# Revit family: Legrand Cabinet Plexo³ 12 modules
name_source: partatom
category: Equipement électrique
revit_build: Autodesk Revit 2018 (Build: 20170223_1515(x64)
units: mm (PartAtom-declared; Revit-internal decimal feet)

## family parameters
Basée sur le plan de construction = Non
Configuration du panneau = Deux colonnes, circuits au sein
Cote de connecteur circulaire = Utiliser le diamètre
Couper avec des vides une fois chargée = Non
Numéro OmniClass = 23.80.30.11.17
Partagée = Non
Point de calcul de pièce = Non
Titre OmniClass = Distribution Boards and Control Panels
Toujours verticalement = Oui
Type d'élément = Tableau de raccordement

## types (16) — shared parameters
ETIM Class 6.0 = EC000214
Fabricant = Legrand
General Conditions of Use = https://export.legrand.com
IK = 09
IP = 65
Image du type = Plexo3_12_modules_001922_pw_153883_pz_0.jpg
Material = Polystyrene
Polystyrene
RAL = 7046
URL = www.legrand.fr

## per-type parameters (varying)
| type | Cabinet 001921 | Cabinet 001922 | Cabinet 001923 | Cabinet 601831 | Cabinet 601832 | Cabinet 601833 | Cabinet 601940 | Cabinet 601941 | Cabinet 601942 | Cabinet 601943 | Cabinet 601961 | Cabinet 601962 | Cabinet 601963 | Cabinet 601981 | Cabinet 601982 | Cabinet 601983 | Terminal block E | Terminal block N |
| Plexo³ 12 modules 1 row 001921 | Oui | Non | Non | Non | Non | Non | Non | Non | Non | Non | Non | Non | Non | Non | Non | Non | terminal block 5+9 holes |  |
| Plexo³ 12 modules 2 rows 001922 | Non | Oui | Non | Non | Non | Non | Non | Non | Non | Non | Non | Non | Non | Non | Non | Non | terminal block 5+18 holes |  |
| Plexo³ 12 modules 3 rows 001923 | Non | Non | Oui | Non | Non | Non | Non | Non | Non | Non | Non | Non | Non | Non | Non | Non | terminal block 5+27 holes |  |
| Plexo³ 12 modules 1 row 601831 | Non | Non | Non | Oui | Non | Non | Non | Non | Non | Non | Non | Non | Non | Non | Non | Non | terminal block 5+9 holes |  |
| Plexo³ 12 modules 1 row 601940 | Non | Non | Non | Non | Non | Non | Oui | Non | Non | Non | Non | Non | Non | Non | Non | Non |  |  |
| Plexo³ 12 modules 1 row 601941 | Non | Non | Non | Non | Non | Non | Non | Oui | Non | Non | Non | Non | Non | Non | Non | Non | terminal block 13 holes | terminal block 8 holes |
| Plexo³ 12 modules 1 row 601961 | Non | Non | Non | Non | Non | Non | Non | Non | Non | Non | Oui | Non | Non | Non | Non | Non | terminal block 13 holes |  |
| Plexo³ 12 modules 1 row 601981 | Non | Non | Non | Non | Non | Non | Non | Non | Non | Non | Non | Non | Non | Oui | Non | Non | terminal block 13 holes | terminal block 13 holes |
| Plexo³ 12 modules 2 rows 601832 | Non | Non | Non | Non | Oui | Non | Non | Non | Non | Non | Non | Non | Non | Non | Non | Non | terminal block 5+18 holes |  |
| Plexo³ 12 modules 2 rows 601942 | Non | Non | Non | Non | Non | Non | Non | Non | Oui | Non | Non | Non | Non | Non | Non | Non |  |  |
| Plexo³ 12 modules 2 rows 601962 | Non | Non | Non | Non | Non | Non | Non | Non | Non | Non | Non | Oui | Non | Non | Non | Non | terminal block 17 holes |  |
| Plexo³ 12 modules 2 rows 601982 | Non | Non | Non | Non | Non | Non | Non | Non | Non | Non | Non | Non | Non | Non | Oui | Non | terminal block 17 holes | terminal block 17 holes |
| Plexo³ 12 modules 3 rows 601833 | Non | Non | Non | Non | Non | Oui | Non | Non | Non | Non | Non | Non | Non | Non | Non | Non | terminal block 5+27 holes |  |
| Plexo³ 12 modules 3 rows 601943 | Non | Non | Non | Non | Non | Non | Non | Non | Non | Oui | Non | Non | Non | Non | Non | Non |  |  |
| Plexo³ 12 modules 3 rows 601963 | Non | Non | Non | Non | Non | Non | Non | Non | Non | Non | Non | Non | Oui | Non | Non | Non | terminal block 22 holes |  |
| Plexo³ 12 modules 3 rows 601983 | Non | Non | Non | Non | Non | Non | Non | Non | Non | Non | Non | Non | Non | Non | Non | Oui | terminal block 22 holes | terminal block 22 holes |

note: column(s) folded — value = type name in every type: Description
